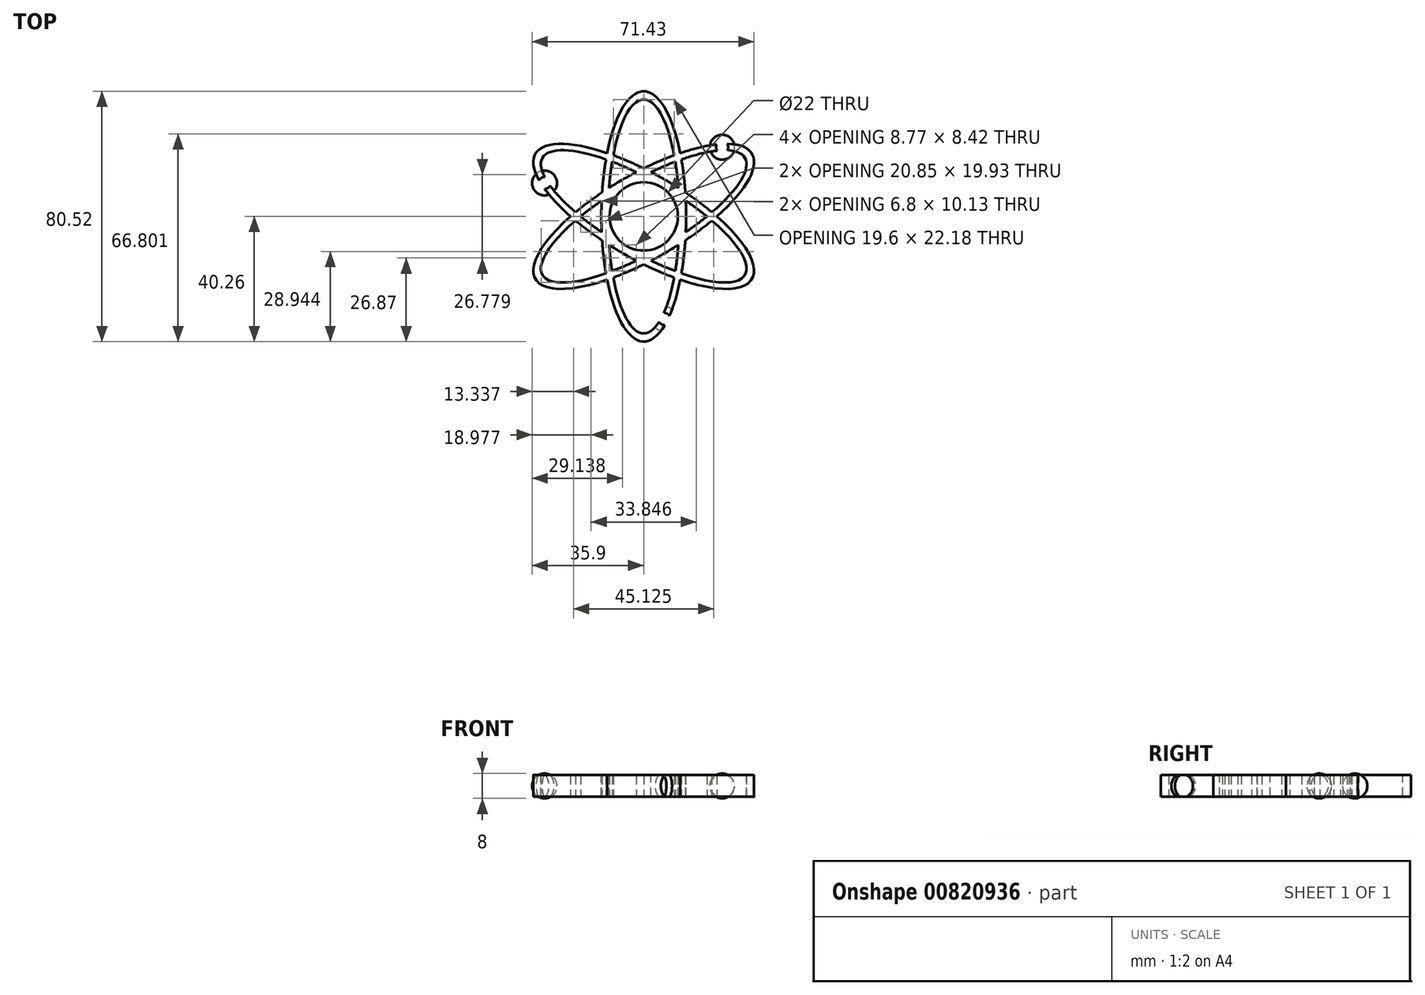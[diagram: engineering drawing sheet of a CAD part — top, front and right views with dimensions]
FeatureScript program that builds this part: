
annotation { "Feature Type Name" : "Feature", "Feature Type Description" : "" }
export const myFeature = defineFeature(function(context is Context, id is Id, definition is map)
    precondition{}
    {
        {
            var Q0;
            Q0=qCreatedBy(makeId("Top.planeOp"),FACE);
            var sketch = newSketch(context, id + "F0", { "sketchPlane" : qUnion([Q0])});
            skCircle(sketch, "E0", {"center": v(0, 0) * mm, "radius": 40.5 * mm, "construction": true});
            skCircle(sketch, "E1", {"center": v(0, 0) * mm, "radius": 11 * mm});
            skEllipticalArc(sketch, "E2", {});
            skEllipticalArc(sketch, "E3.1.0", {});
            skEllipticalArc(sketch, "E3.1.1", {});
            skEllipticalArc(sketch, "E3.2.0", {});
            skEllipticalArc(sketch, "E3.2.1", {});
            skEllipticalArc(sketch, "E4.trimOffspring", {});
            skEllipticalArc(sketch, "E5.trimOffspring", {});
            skEllipticalArc(sketch, "E6.trimOffspring", {});
            skEllipticalArc(sketch, "E7.trimOffspring", {});
            skEllipticalArc(sketch, "E8.trimOffspring", {});
            skEllipticalArc(sketch, "E9.trimOffspring", {});
            skEllipticalArc(sketch, "E10.trimOffspring", {});
            skEllipticalArc(sketch, "E11.trimOffspring", {});
            skEllipticalArc(sketch, "E12.trimOffspring", {});
            skEllipticalArc(sketch, "E13.trimOffspring", {});
            skEllipticalArc(sketch, "E14.trimOffspring", {});
            skEllipticalArc(sketch, "E15.trimOffspring", {});
            skEllipticalArc(sketch, "E16.trimOffspring", {});
            skEllipticalArc(sketch, "E17.trimOffspring", {});
            skEllipticalArc(sketch, "E18.trimOffspring", {});
            skEllipticalArc(sketch, "E19.trimOffspring", {});
            skEllipticalArc(sketch, "E20.trimOffspring", {});
            skEllipticalArc(sketch, "E21.trimOffspring", {});
            skEllipticalArc(sketch, "E22.trimOffspring", {});
            skEllipticalArc(sketch, "E23.trimOffspring", {});
            skEllipticalArc(sketch, "E24.trimOffspring", {});
            skEllipticalArc(sketch, "E25.trimOffspring", {});
            skEllipticalArc(sketch, "E26.trimOffspring", {});
            skEllipticalArc(sketch, "E27.trimOffspring", {});
            skEllipticalArc(sketch, "E28.trimOffspring", {});
            skEllipticalArc(sketch, "E29.trimOffspring", {});
            skEllipticalArc(sketch, "E30.trimOffspring", {});
            skEllipticalArc(sketch, "E31.trimOffspring", {});
            skEllipticalArc(sketch, "E32.trimOffspring", {});
            skEllipticalArc(sketch, "E33.trimOffspring", {});
            skEllipticalArc(sketch, "E34.trimOffspring", {});
            skEllipticalArc(sketch, "E35.trimOffspring", {});
            skEllipticalArc(sketch, "E36.trimOffspring", {});
            skEllipticalArc(sketch, "E37.trimOffspring", {});
            skEllipticalArc(sketch, "E38.trimOffspring", {});
            skEllipticalArc(sketch, "E39.trimOffspring", {});
            skEllipticalArc(sketch, "E40.trimOffspring", {});
            const initialGuessF0  = {"E2": [0, 0, 0, -1, 0.0402606725692749, 0.0136325, 4.586270794180662, 4.838507166588717], "E3.1.0": [0, 0, 0.8660254037844388, 0.5, 0.037632599999999995, 0.011495072052671739, 2.1209241219030113, 4.162261185276575], "E3.1.1": [0, 0, 0.8660254037844388, 0.5, 0.0402606725692749, 0.0136325, 2.101217242693888, 4.181968064485698], "E3.2.0": [0, 0, -0.8660254037844384, 0.5, 0.037632599999999995, 0.011495072052671739, 1.0841688714158986, 1.3243656933408008], "E3.2.1": [0, 0, -0.8660254037844384, 0.5, 0.0402606725692749, 0.0136325, 1.0982924268704228, 1.377737007437074], "E4.trimOffspring": [0, 0, 0.8660254037844388, 0.5, 0.037632599999999995, 0.011495072052671739, 1.817226960248993, 2.0574237821738945], "E5.trimOffspring": [0, 0, 0.8660254037844388, 0.5, 0.0402606725692749, 0.0136325, 1.4446781405908693, 1.6969145129989247], "E6.trimOffspring": [0, 0, -0.8660254037844384, 0.5, 0.0402606725692749, 0.0136325, 4.9054482997425115, 5.184892880309164], "E7.trimOffspring": [0, 0, -0.8660254037844384, 0.5, 0.037632599999999995, 0.011495072052671739, 4.958819613838786, 5.1990164357636885], "E8.trimOffspring": [0, 0, 0, -1, 0.037632599999999995, 0.011495072052671739, 1.817226960248993, 2.0574237821738945], "E9.trimOffspring": [0, 0, 0.8660254037844388, 0.5, 0.037632599999999995, 0.011495072052671739, 4.958819613838785, 5.199016435763688], "E10.trimOffspring": [0, 0, -0.8660254037844384, 0.5, 0.037632599999999995, 0.011495072052671739, 1.8172269602489926, 2.0574237821738945], "E11.trimOffspring": [0, 0, 0, -1, 0.037632599999999995, 0.011495072052671739, 4.958819613838785, 5.199016435763688], "E12.trimOffspring": [0, 0, 0.8660254037844388, 0.5, 0.0402606725692749, 0.0136325, 1.763855646152719, 2.0433002267193703], "E13.trimOffspring": [0, 0, 0, -1, 0.0402606725692749, 0.0136325, 1.7638556461527202, 2.0433002267193703], "E14.trimOffspring": [0, 0, -0.8660254037844384, 0.5, 0.0402606725692749, 0.0136325, 4.586270794180662, 4.838507166588716], "E15.trimOffspring": [0, 0, 0, -1, 0.0402606725692749, 0.0136325, 1.4446781405908684, 1.6969145129989238], "E16.trimOffspring": [0, 0, 0.8660254037844388, 0.5, 0.0402606725692749, 0.0136325, 4.9054482997425115, 5.184892880309164], "E17.trimOffspring": [0, 0, -0.8660254037844384, 0.5, 0.0402606725692749, 0.0136325, 1.7638556461527193, 2.0433002267193707], "E18.trimOffspring": [0, 0, 0.8660254037844388, 0.5, 0.0402606725692749, 0.0136325, 4.5862707941806615, 4.838507166588718], "E19.trimOffspring": [0, 0, -0.8660254037844384, 0.5, 0.0402606725692749, 0.0136325, 1.444678140590869, 1.696914512998924], "E20.trimOffspring": [0, 0, 0, -1, 0.0402606725692749, 0.0136325, 4.9054482997425115, 5.184892880309164], "E21.trimOffspring": [0, 0, 0.8660254037844388, 0.5, 0.037632599999999995, 0.011495072052671739, 4.225761525005691, 4.465958346930594], "E22.trimOffspring": [0, 0, 0, -1, 0.037632599999999995, 0.011495072052671739, 5.262516775492804, 1.0206685316867823], "E23.trimOffspring": [0, 0, 0.8660254037844388, 0.5, 0.0402606725692749, 0.0136325, 4.2398850804602155, 4.519329661026868], "E24.trimOffspring": [0, 0, 0, -1, 0.0402606725692749, 0.0136325, 5.242809896283681, 1.040375410895905], "E25.trimOffspring": [0, 0, 0, -1, 0.037632599999999995, 0.011495072052671739, 1.0841688714158986, 1.324365693340801], "E26.trimOffspring": [0, 0, -0.8660254037844384, 0.5, 0.037632599999999995, 0.011495072052671739, 2.1209241219030113, 4.162261185276575], "E27.trimOffspring": [0, 0, 0, -1, 0.0402606725692749, 0.0136325, 1.0982924268704224, 1.3777370074370738], "E28.trimOffspring": [0, 0, -0.8660254037844384, 0.5, 0.0402606725692749, 0.0136325, 2.101217242693888, 4.181968064485698], "E29.trimOffspring": [0, 0, -0.8660254037844384, 0.5, 0.037632599999999995, 0.011495072052671739, 4.225761525005691, 4.465958346930594], "E30.trimOffspring": [0, 0, 0.8660254037844388, 0.5, 0.0402606725692749, 0.0136325, 5.242809896283681, 1.040375410895905], "E31.trimOffspring": [0, 0, -0.8660254037844384, 0.5, 0.0402606725692749, 0.0136325, 4.2398850804602155, 4.519329661026868], "E32.trimOffspring": [0, 0, 0.8660254037844388, 0.5, 0.037632599999999995, 0.011495072052671739, 5.262516775492804, 1.0206685316867823], "E33.trimOffspring": [0, 0, 0, -1, 0.0402606725692749, 0.0136325, 2.1012172426938878, 4.181968064485698], "E34.trimOffspring": [0, 0, 0.8660254037844388, 0.5, 0.0402606725692749, 0.0136325, 1.0982924268704224, 1.3777370074370747], "E35.trimOffspring": [0, 0, 0, -1, 0.037632599999999995, 0.011495072052671739, 2.1209241219030117, 4.162261185276574], "E36.trimOffspring": [0, 0, 0.8660254037844388, 0.5, 0.037632599999999995, 0.011495072052671739, 1.0841688714158986, 1.3243656933408001], "E37.trimOffspring": [0, 0, 0, -1, 0.037632599999999995, 0.011495072052671739, 4.225761525005691, 4.465958346930595], "E38.trimOffspring": [0, 0, -0.8660254037844384, 0.5, 0.0402606725692749, 0.0136325, 5.242809896283681, 1.0403754108959054], "E39.trimOffspring": [0, 0, 0, -1, 0.0402606725692749, 0.0136325, 4.2398850804602155, 4.519329661026868], "E40.trimOffspring": [0, 0, -0.8660254037844384, 0.5, 0.037632599999999995, 0.011495072052671739, 5.262516775492805, 1.020668531686782]};
            skSetInitialGuess(sketch, initialGuessF0);
            skSolve(sketch);
        }
        {
            var Q0;
            Q0 = qSketchRegion(id + "F0", true);
            extrude(context, id + "F1", {"entities" : qUnion([Q0]), "endBound" : BoundingType.SYMMETRIC, "depth" : 7 * mm, "offsetDistance" : 25 * mm});
        }
        {
            var Q0;
            Q0=qCreatedBy(makeId("Top.planeOp"),FACE);
            var sketch = newSketch(context, id + "F2", { "sketchPlane" : qUnion([Q0])});
            skArc(sketch, "E41", {"start": v(6.64, -37) * mm, "mid": v(10.64, -33) * mm, "end": v(6.64, -29) * mm});
            skPoint(sketch, "E42.center", {"position": v(0, 0) * mm});
            skLineSegment(sketch, "E43", {"start": v(6.64, -33) * mm, "end": v(6.64, -41.87) * mm});
            skLineSegment(sketch, "E44", {"start": v(6.64, -33) * mm, "end": v(6.64, -26.72) * mm});
            skLineSegment(sketch, "E45.1.0", {"start": v(25.26, 22.25) * mm, "end": v(32.94, 26.69) * mm});
            skLineSegment(sketch, "E45.1.1", {"start": v(25.26, 22.25) * mm, "end": v(19.81, 19.1) * mm});
            skArc(sketch, "E45.1.2", {"start": v(28.72, 24.25) * mm, "mid": v(23.26, 25.72) * mm, "end": v(21.8, 20.25) * mm});
            skLineSegment(sketch, "E45.2.0", {"start": v(-31.9, 10.75) * mm, "end": v(-39.58, 15.18) * mm});
            skLineSegment(sketch, "E45.2.1", {"start": v(-31.9, 10.75) * mm, "end": v(-26.46, 7.6) * mm});
            skArc(sketch, "E45.2.2", {"start": v(-35.36, 12.75) * mm, "mid": v(-33.9, 7.28) * mm, "end": v(-28.44, 8.75) * mm});
            skSolve(sketch);
        }
        {
            var Q0;
            {var subQ0=sQuery(id+"F2.wireOp",EDGE,"E41");Q0=makeQuery(id+"F2.imprint","IMPRINT",FACE,{"disambiguationData":[TD([[makeQuery(id+"F2.imprint","IMPRINT",EDGE,{"derivedFrom":subQ0}),1.0]])]});}
            var Q1;
            Q1=sQuery(id+"F2.wireOp",EDGE,"E43");
            revolve(context, id + "F3", {"surfaceOperationType" : NewSurfaceOperationType.NEW, "entities" : qUnion([Q0]), "axis" : qUnion([Q1]), "revolveType" : RevolveType.FULL});
        }
        {
            var Q0;
            {var subQ3=sQuery(id+"F2.wireOp",EDGE,"E45.2.2");Q0=makeQuery(id+"F2.imprint","IMPRINT",FACE,{"disambiguationData":[TD([[makeQuery(id+"F2.imprint","IMPRINT",EDGE,{"derivedFrom":subQ3}),1.0]])]});}
            var Q1;
            Q1=sQuery(id+"F2.wireOp",EDGE,"E45.2.0");
            revolve(context, id + "F4", {"operationType" : NewBodyOperationType.ADD, "surfaceOperationType" : NewSurfaceOperationType.NEW, "entities" : qUnion([Q0]), "axis" : qUnion([Q1]), "revolveType" : RevolveType.FULL});
        }
        {
            var Q0;
            {var subQ3=sQuery(id+"F2.wireOp",EDGE,"E45.1.2");Q0=makeQuery(id+"F2.imprint","IMPRINT",FACE,{"disambiguationData":[TD([[makeQuery(id+"F2.imprint","IMPRINT",EDGE,{"derivedFrom":subQ3}),1.0]])]});}
            var Q1;
            Q1=sQuery(id+"F2.wireOp",EDGE,"E45.1.0");
            revolve(context, id + "F5", {"operationType" : NewBodyOperationType.ADD, "surfaceOperationType" : NewSurfaceOperationType.NEW, "entities" : qUnion([Q0]), "axis" : qUnion([Q1]), "revolveType" : RevolveType.FULL});
        }
        {
            var Q0;
            Q0=makeQuery(id+"F4.opRevolve","SWEPT_BODY",BODY,{"disambiguationData":[OSD([sQuery(id+"F2.wireOp",EDGE,"E45.2.0"),sQuery(id+"F2.wireOp",EDGE,"E45.2.1"),sQuery(id+"F2.wireOp",EDGE,"E45.2.2")])]});
            var Q1;
            Q1=makeQuery(id+"F5.opRevolve","SWEPT_BODY",BODY,{"disambiguationData":[OSD([sQuery(id+"F2.wireOp",EDGE,"E45.1.0"),sQuery(id+"F2.wireOp",EDGE,"E45.1.1"),sQuery(id+"F2.wireOp",EDGE,"E45.1.2")])]});
            var Q2;
            Q2=makeQuery(id+"F3.opRevolve","SWEPT_BODY",BODY,{"disambiguationData":[OSD([sQuery(id+"F2.wireOp",EDGE,"E41"),sQuery(id+"F2.wireOp",EDGE,"E43"),sQuery(id+"F2.wireOp",EDGE,"E44")])]});
            var Q3;
            Q3=makeQuery(id+"F1.opExtrude","SWEPT_BODY",BODY,{"disambiguationData":[OSD([sQuery(id+"F0.wireOp",EDGE,"E1"),sQuery(id+"F0.wireOp",EDGE,"E2"),sQuery(id+"F0.wireOp",EDGE,"E3.1.0"),sQuery(id+"F0.wireOp",EDGE,"E3.1.1"),sQuery(id+"F0.wireOp",EDGE,"E3.2.0"),sQuery(id+"F0.wireOp",EDGE,"E3.2.1"),sQuery(id+"F0.wireOp",EDGE,"E4.trimOffspring"),sQuery(id+"F0.wireOp",EDGE,"E5.trimOffspring"),sQuery(id+"F0.wireOp",EDGE,"E6.trimOffspring"),sQuery(id+"F0.wireOp",EDGE,"E7.trimOffspring"),sQuery(id+"F0.wireOp",EDGE,"E8.trimOffspring"),sQuery(id+"F0.wireOp",EDGE,"E9.trimOffspring"),sQuery(id+"F0.wireOp",EDGE,"E10.trimOffspring"),sQuery(id+"F0.wireOp",EDGE,"E11.trimOffspring"),sQuery(id+"F0.wireOp",EDGE,"E12.trimOffspring"),sQuery(id+"F0.wireOp",EDGE,"E13.trimOffspring"),sQuery(id+"F0.wireOp",EDGE,"E14.trimOffspring"),sQuery(id+"F0.wireOp",EDGE,"E15.trimOffspring"),sQuery(id+"F0.wireOp",EDGE,"E16.trimOffspring"),sQuery(id+"F0.wireOp",EDGE,"E17.trimOffspring"),sQuery(id+"F0.wireOp",EDGE,"E18.trimOffspring"),sQuery(id+"F0.wireOp",EDGE,"E19.trimOffspring"),sQuery(id+"F0.wireOp",EDGE,"E20.trimOffspring"),sQuery(id+"F0.wireOp",EDGE,"E21.trimOffspring"),sQuery(id+"F0.wireOp",EDGE,"E22.trimOffspring"),sQuery(id+"F0.wireOp",EDGE,"E23.trimOffspring"),sQuery(id+"F0.wireOp",EDGE,"E24.trimOffspring"),sQuery(id+"F0.wireOp",EDGE,"E25.trimOffspring"),sQuery(id+"F0.wireOp",EDGE,"E26.trimOffspring"),sQuery(id+"F0.wireOp",EDGE,"E27.trimOffspring"),sQuery(id+"F0.wireOp",EDGE,"E28.trimOffspring"),sQuery(id+"F0.wireOp",EDGE,"E29.trimOffspring"),sQuery(id+"F0.wireOp",EDGE,"E30.trimOffspring"),sQuery(id+"F0.wireOp",EDGE,"E31.trimOffspring"),sQuery(id+"F0.wireOp",EDGE,"E32.trimOffspring"),sQuery(id+"F0.wireOp",EDGE,"E33.trimOffspring"),sQuery(id+"F0.wireOp",EDGE,"E34.trimOffspring"),sQuery(id+"F0.wireOp",EDGE,"E35.trimOffspring"),sQuery(id+"F0.wireOp",EDGE,"E36.trimOffspring"),sQuery(id+"F0.wireOp",EDGE,"E37.trimOffspring"),sQuery(id+"F0.wireOp",EDGE,"E38.trimOffspring"),sQuery(id+"F0.wireOp",EDGE,"E39.trimOffspring"),sQuery(id+"F0.wireOp",EDGE,"E40.trimOffspring")])]});
            booleanBodies(context, id + "F6", {"operationType" : BooleanOperationType.SUBTRACTION, "tools" : qUnion([Q0, Q1, Q2]), "targets" : qUnion([Q3])});
        }
    });
